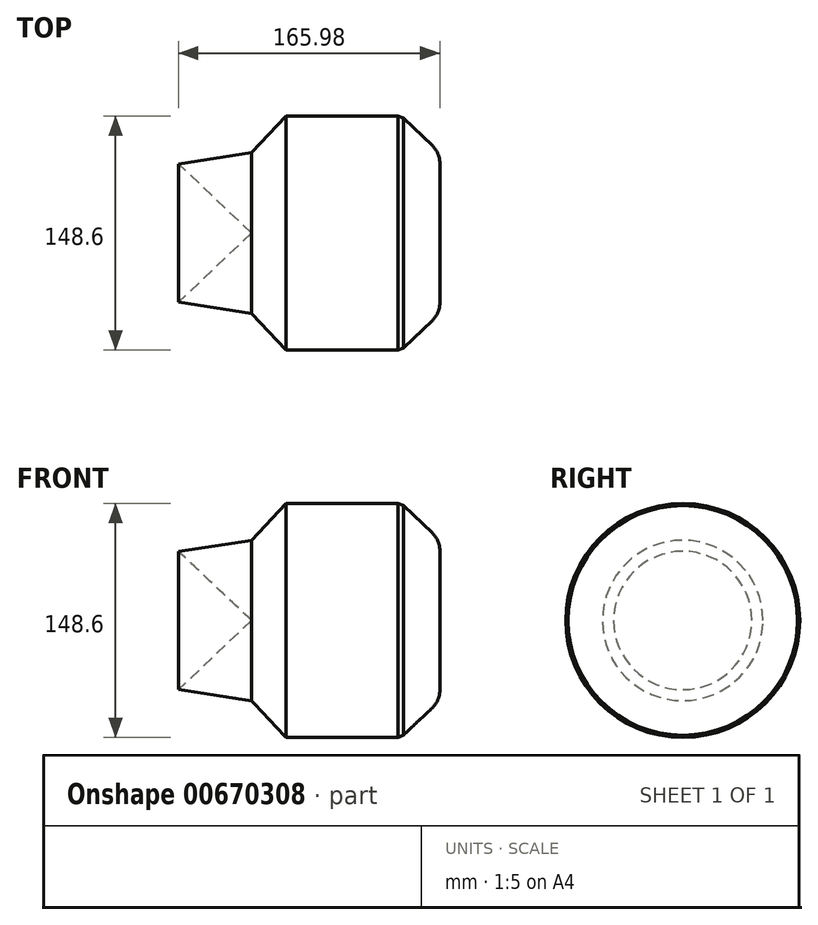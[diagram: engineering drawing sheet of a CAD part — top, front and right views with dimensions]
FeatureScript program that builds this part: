
annotation { "Feature Type Name" : "Feature", "Feature Type Description" : "" }
export const myFeature = defineFeature(function(context is Context, id is Id, definition is map)
    precondition{}
    {
        {
            var Q0;
            Q0=qCreatedBy(makeId("Top.planeOp"),FACE);
            var sketch = newSketch(context, id + "F0", { "sketchPlane" : qUnion([Q0])});
            skLineSegment(sketch, "E0", {"start": v(0, 0) * mm, "end": v(0, 50.97) * mm});
            skLineSegment(sketch, "E1", {"start": v(0, 50.97) * mm, "end": v(22.11, 74.3) * mm});
            skLineSegment(sketch, "E2", {"start": v(22.11, 74.3) * mm, "end": v(95.02, 74.3) * mm});
            skLineSegment(sketch, "E3", {"start": v(95.02, 74.3) * mm, "end": v(119.63, 50.97) * mm});
            skLineSegment(sketch, "E4", {"start": v(119.63, 50.97) * mm, "end": v(119.63, 0) * mm});
            skLineSegment(sketch, "E5", {"start": v(119.63, 0) * mm, "end": v(0, 0) * mm});
            skLineSegment(sketch, "E6", {"start": v(0, 0) * mm, "end": v(-46.35, 43.94) * mm});
            skLineSegment(sketch, "E7", {"start": v(-46.35, 43.94) * mm, "end": v(0, 50.97) * mm});
            skSolve(sketch);
        }
        {
            var Q0;
            Q0=makeQuery(id+"F0.imprint","IMPRINT",FACE,{"disambiguationData":[TD([[makeQuery(id+"F0.imprint","IMPRINT",EDGE,{"derivedFrom":sQuery(id+"F0.wireOp",EDGE,"E0")}),1.0]])]});
            var Q1;
            Q1=makeQuery(id+"F0.imprint","IMPRINT",FACE,{"disambiguationData":[TD([[makeQuery(id+"F0.imprint","IMPRINT",EDGE,{"derivedFrom":sQuery(id+"F0.wireOp",EDGE,"E0")}),-1.0]])]});
            var Q2;
            Q2=sQuery(id+"F0.wireOp",EDGE,"E5");
            revolve(context, id + "F1", {"entities" : qUnion([Q0, Q1]), "axis" : qUnion([Q2]), "revolveType" : RevolveType.FULL});
        }
        {
            var Q0;
            Q0=makeQuery(id+"F1.opRevolve","SWEPT_EDGE",EDGE,{"disambiguationData":[OSD([sQuery(id+"F0.wireOp",EDGE,"E2"),sQuery(id+"F0.wireOp",EDGE,"E3")])]});
            chamfer(context, id + "F2", {"entities" : qUnion([Q0]), "width" : 5.08 * mm, "tangentPropagation" : true});
        }
        {
            var Q0;
            Q0=makeQuery(id+"F1.opRevolve","SWEPT_EDGE",EDGE,{"disambiguationData":[OSD([sQuery(id+"F0.wireOp",EDGE,"E3"),sQuery(id+"F0.wireOp",EDGE,"E4")])]});
            fillet(context, id + "F3", {"entities" : qUnion([Q0]), "radius" : 15.24 * mm, "tangentPropagation" : true, "allowEdgeOverflow" : false});
        }
    });
